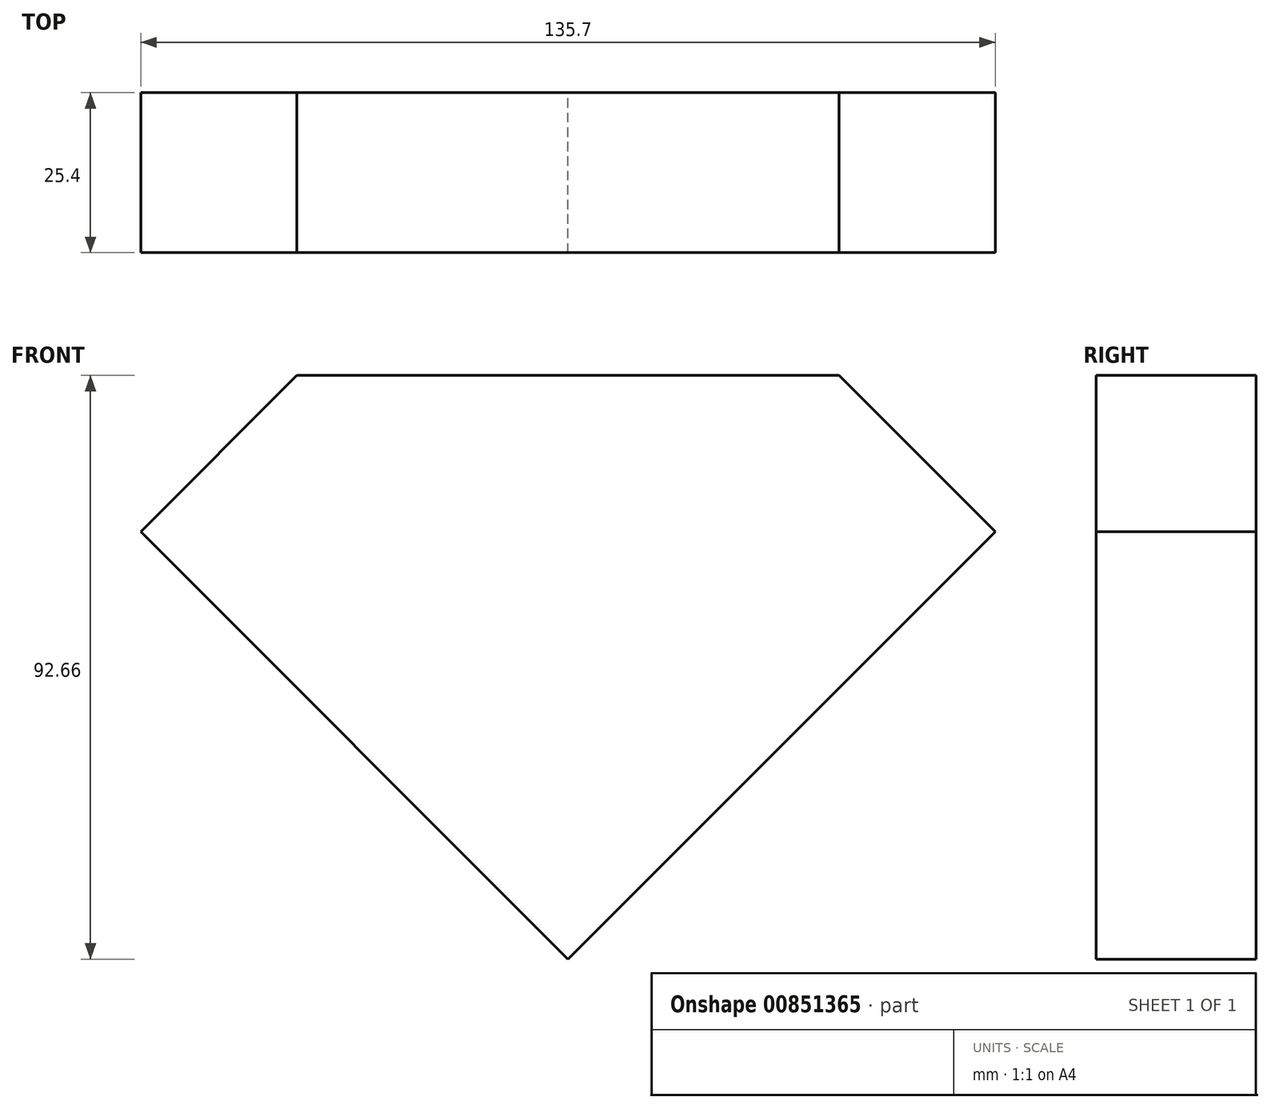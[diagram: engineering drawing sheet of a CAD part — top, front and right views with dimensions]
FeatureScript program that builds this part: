
annotation { "Feature Type Name" : "Feature", "Feature Type Description" : "" }
export const myFeature = defineFeature(function(context is Context, id is Id, definition is map)
    precondition{}
    {
        {
            var Q0;
            Q0=qCreatedBy(makeId("Front.planeOp"),FACE);
            var sketch = newSketch(context, id + "F0", { "sketchPlane" : qUnion([Q0])});
            skLineSegment(sketch, "E0", {"start": v(-43.04, 92.66) * mm, "end": v(-67.85, 67.85) * mm});
            skLineSegment(sketch, "E1", {"start": v(-67.85, 67.85) * mm, "end": v(0, 0) * mm});
            skLineSegment(sketch, "E2", {"start": v(0, 0) * mm, "end": v(67.85, 67.85) * mm});
            skLineSegment(sketch, "E3", {"start": v(67.85, 67.85) * mm, "end": v(43.04, 92.66) * mm});
            skLineSegment(sketch, "E4", {"start": v(43.04, 92.66) * mm, "end": v(-43.04, 92.66) * mm});
            skSolve(sketch);
        }
        {
            var Q0;
            Q0=makeQuery(id+"F0.imprint","IMPRINT",FACE,{"disambiguationData":[TD([[makeQuery(id+"F0.imprint","IMPRINT",EDGE,{"derivedFrom":sQuery(id+"F0.wireOp",EDGE,"E0")}),1.0]])]});
            var Q1;
            Q1=sQuery(id+"F0.wireOp",EDGE,"E2");
            var Q2;
            Q2=sQuery(id+"F0.wireOp",EDGE,"E1");
            var Q3;
            Q3=sQuery(id+"F0.wireOp",EDGE,"E0");
            var Q4;
            Q4=sQuery(id+"F0.wireOp",EDGE,"E4");
            var Q5;
            Q5=sQuery(id+"F0.wireOp",EDGE,"E3");
            extrude(context, id + "F1", {"entities" : qUnion([Q0]), "surfaceEntities" : qUnion([Q1, Q2, Q3, Q4, Q5]), "depth" : 25.4 * mm, "offsetDistance" : 25.4 * mm});
        }
    });
